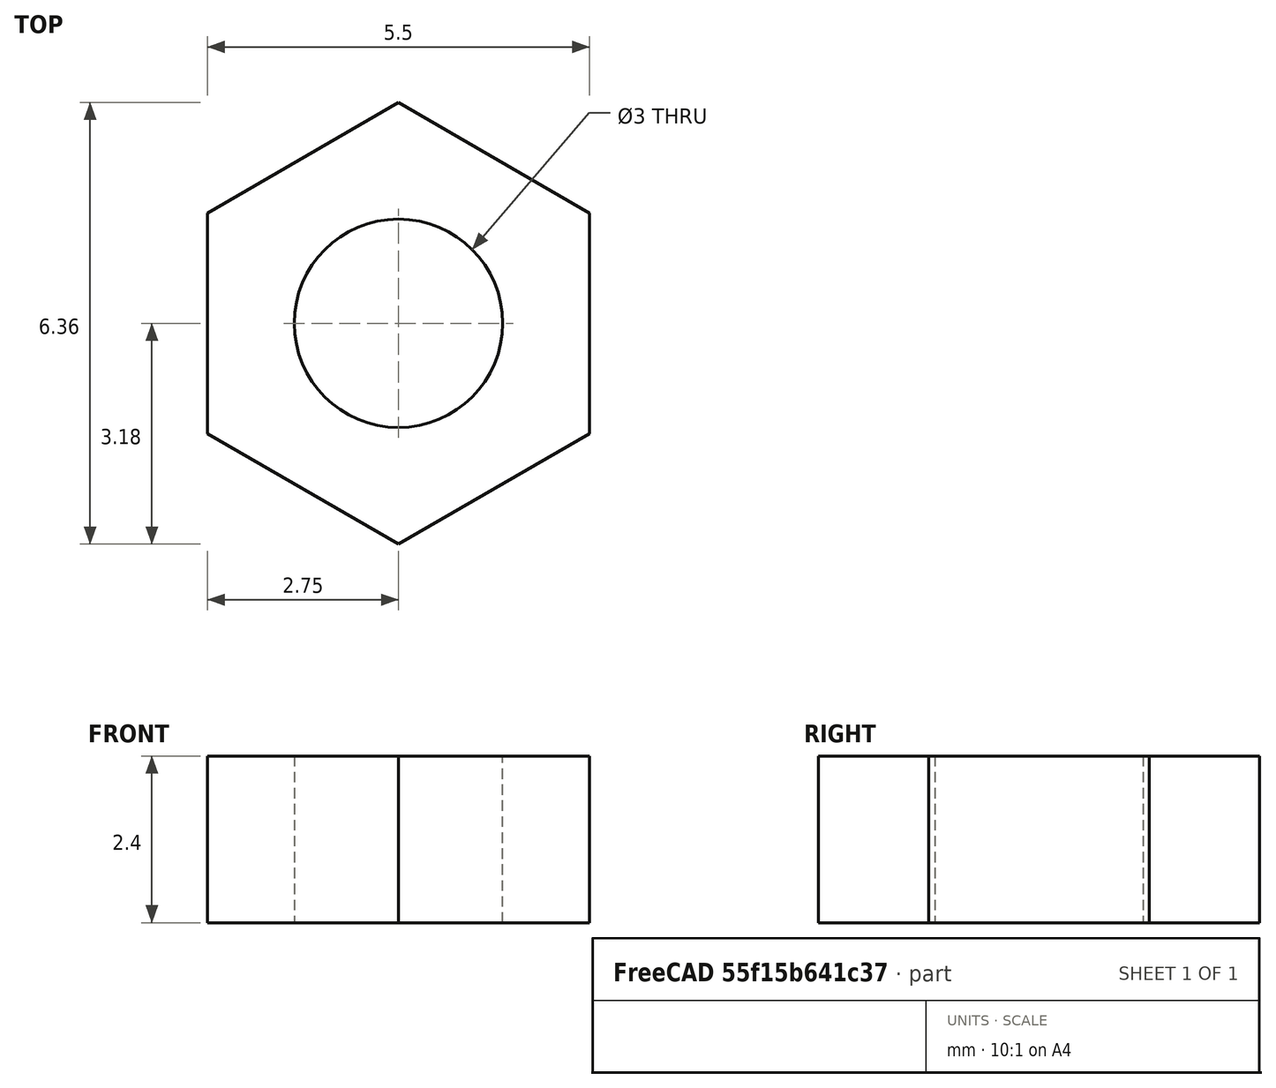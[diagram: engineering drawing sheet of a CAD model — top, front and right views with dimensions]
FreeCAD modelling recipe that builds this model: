
FCSTD DOCUMENT  (FreeCAD 0.18R14555 (Git shallow))
Label: m3-nut
License: All rights reserved
LicenseURL: http://en.wikipedia.org/wiki/All_rights_reserved
objects: Sketcher::SketchObject×1, PartDesign::Pad×1, PartDesign::Body×1
note: 4 computed .brp shape members not serialized (recipe doc carries the construction recipe); baked Part::Feature solids carry a one-line shape summary decoded from their .brp

FEATURE [Sketcher::SketchObject] Sketch
  MapMode = 5
  Support = -> [XY_Plane]
  sketch-geometry (8):
    g0: LineSegment StartX=0 StartY=3.17543 StartZ=0 EndX=-2.75 EndY=1.58771 EndZ=0
    g1: LineSegment StartX=-2.75 StartY=1.58771 StartZ=0 EndX=-2.75 EndY=-1.58771 EndZ=0
    g2: LineSegment StartX=-2.75 StartY=-1.58771 StartZ=0 EndX=6.3736e-12 EndY=-3.17543 EndZ=0
    g3: LineSegment StartX=6.3736e-12 StartY=-3.17543 StartZ=0 EndX=2.75 EndY=-1.58771 EndZ=0
    g4: LineSegment StartX=2.75 StartY=-1.58771 StartZ=0 EndX=2.75 EndY=1.58771 EndZ=0
    g5: LineSegment StartX=2.75 StartY=1.58771 StartZ=0 EndX=0 EndY=3.17543 EndZ=0
    g6: Circle [constr] CenterX=0 CenterY=0 CenterZ=0 NormalX=0 NormalY=0 NormalZ=1 AngleXU=0 Radius=3.17543
    g7: Circle CenterX=0 CenterY=0 CenterZ=0 NormalX=0 NormalY=0 NormalZ=1 AngleXU=0 Radius=1.5
  constraints (18):
    c: Coincident(g0,g1)
    c: Coincident(g1,g2)
    c: Coincident(g2,g3)
    c: Coincident(g3,g4)
    c: Coincident(g4,g5)
    c: Coincident(g5,g0)
    c: Equal(g0, g1-g5) x5
    c: PointOnObject(g0,g6)
    c: PointOnObject(g1,g6)
    c: PointOnObject(g2,g6)
    c: PointOnObject(g3,g6)
    c: PointOnObject(g4,g6)
    c: PointOnObject(g5,g6)
    c: Coincident(g6,g-1)
    c: PointOnObject(g5,g-2)
    c: DistanceX(g0,g4) = 5.5
    c: Coincident(g7,g-1)
    c: Radius(g7) = 1.5
FEATURE [PartDesign::Pad] Pad
  Length = 2.4
  Length2 = 100
  Profile = -> Sketch
  Type = 0
FEATURE [PartDesign::Body] Body
  Group = -> [Sketch,Pad]
  Origin = -> Origin
  Tip = -> Pad
